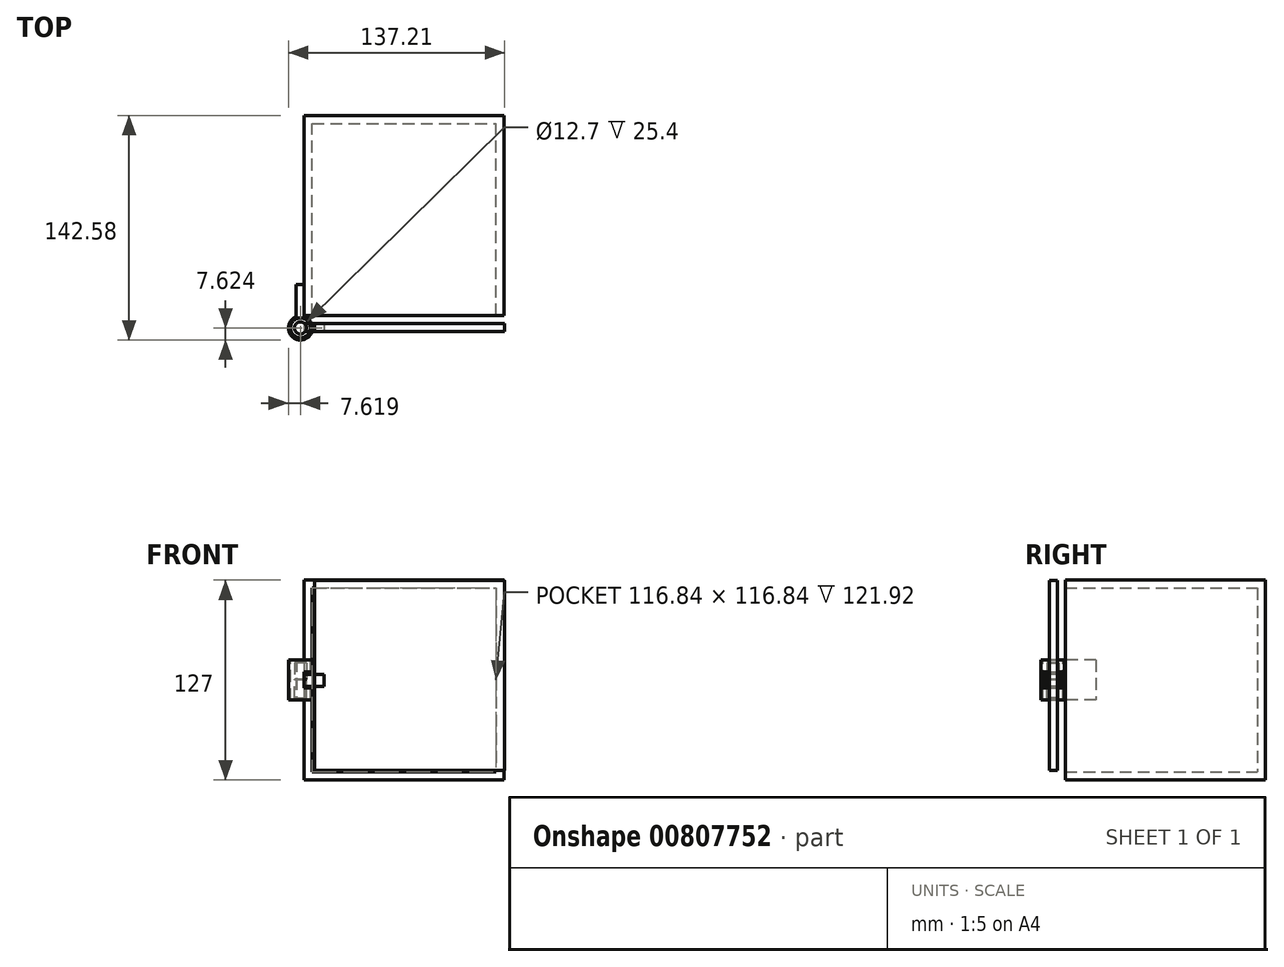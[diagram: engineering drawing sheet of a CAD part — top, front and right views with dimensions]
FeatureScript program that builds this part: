
annotation { "Feature Type Name" : "Feature", "Feature Type Description" : "" }
export const myFeature = defineFeature(function(context is Context, id is Id, definition is map)
    precondition{}
    {
        {
            var Q0;
            Q0=qCreatedBy(makeId("Front.planeOp"),FACE);
            var sketch = newSketch(context, id + "F0", { "sketchPlane" : qUnion([Q0])});
            skLineSegment(sketch, "E0.bottom", {"start": v(-62.85, 63) * mm, "end": v(64.15, 63) * mm});
            skLineSegment(sketch, "E0.top", {"start": v(-62.85, -64) * mm, "end": v(64.15, -64) * mm});
            skLineSegment(sketch, "E0.left", {"start": v(-62.85, 63) * mm, "end": v(-62.85, -64) * mm});
            skLineSegment(sketch, "E0.right", {"start": v(64.15, 63) * mm, "end": v(64.15, -64) * mm});
            skSolve(sketch);
        }
        {
            var Q0;
            Q0 = qSketchRegion(id + "F0", true);
            extrude(context, id + "F1", {"entities" : qUnion([Q0]), "depth" : 127 * mm, "offsetDistance" : 25.4 * mm});
        }
        {
            var Q0;
            Q0=makeQuery(id+"F1.opExtrude","CAP_FACE",FACE,{"disambiguationData":[OSD([sQuery(id+"F0.wireOp",EDGE,"E0.bottom"),sQuery(id+"F0.wireOp",EDGE,"E0.top"),sQuery(id+"F0.wireOp",EDGE,"E0.left"),sQuery(id+"F0.wireOp",EDGE,"E0.right")])],"isStart":false});
            shell(context, id + "F2", {"entities" : qUnion([Q0]), "thickness" : 5.08 * mm});
        }
        {
            var Q0;
            Q0=makeQuery(id+"F1.opExtrude","SWEPT_FACE",FACE,{"disambiguationData":[OSD([sQuery(id+"F0.wireOp",EDGE,"E0.left")])]});
            var sketch = newSketch(context, id + "F3", { "sketchPlane" : qUnion([Q0])});
            skLineSegment(sketch, "E1.bottom", {"start": v(107.48, 12.2) * mm, "end": v(127.8, 12.2) * mm});
            skLineSegment(sketch, "E1.top", {"start": v(107.48, -13.2) * mm, "end": v(127.8, -13.2) * mm});
            skLineSegment(sketch, "E1.left", {"start": v(107.48, 12.2) * mm, "end": v(107.48, -13.2) * mm});
            skLineSegment(sketch, "E1.right", {"start": v(127.8, 12.2) * mm, "end": v(127.8, -13.2) * mm});
            skSolve(sketch);
        }
        {
            var Q0;
            Q0 = qSketchRegion(id + "F3", true);
            extrude(context, id + "F4", {"entities" : qUnion([Q0]), "operationType" : NewBodyOperationType.ADD, "depth" : 5.08 * mm, "offsetDistance" : 25.4 * mm});
        }
        {
            var Q0;
            Q0=makeQuery(id+"F4.opExtrude","SWEPT_FACE",FACE,{"disambiguationData":[OSD([sQuery(id+"F3.wireOp",EDGE,"E1.top")])]});
            var sketch = newSketch(context, id + "F5", { "sketchPlane" : qUnion([Q0])});
            skCircle(sketch, "E2", {"center": v(-65.23, 134.96) * mm, "radius": 7.62 * mm});
            skSolve(sketch);
        }
        {
            var Q0;
            Q0 = qSketchRegion(id + "F5", true);
            extrude(context, id + "F6", {"entities" : qUnion([Q0]), "operationType" : NewBodyOperationType.ADD, "oppositeDirection" : true, "depth" : 25.4 * mm, "offsetDistance" : 25.4 * mm});
        }
        {
            var Q0;
            Q0=makeQuery(id+"F6.boolean.opBoolean","MERGE",FACE,{"derivedFrom":[makeQuery(id+"F4.opExtrude","SWEPT_FACE",FACE,{"disambiguationData":[OSD([sQuery(id+"F3.wireOp",EDGE,"E1.bottom")])]}),makeQuery(id+"F6.opExtrude","CAP_FACE",FACE,{"disambiguationData":[OSD([sQuery(id+"F5.wireOp",EDGE,"E2")])],"isStart":false})]});
            var sketch = newSketch(context, id + "F7", { "sketchPlane" : qUnion([Q0])});
            skCircle(sketch, "E3", {"center": v(-65.23, -134.96) * mm, "radius": 6.35 * mm});
            skSolve(sketch);
        }
        {
            var Q0;
            Q0 = qSketchRegion(id + "F7", true);
            extrude(context, id + "F8", {"entities" : qUnion([Q0]), "operationType" : NewBodyOperationType.REMOVE, "oppositeDirection" : true, "depth" : 65.02 * mm, "offsetDistance" : 25.4 * mm});
        }
        {
            var Q0;
            Q0=makeQuery(id+"F1.opExtrude","CAP_FACE",FACE,{"disambiguationData":[OSD([sQuery(id+"F0.wireOp",EDGE,"E0.bottom"),sQuery(id+"F0.wireOp",EDGE,"E0.top"),sQuery(id+"F0.wireOp",EDGE,"E0.left"),sQuery(id+"F0.wireOp",EDGE,"E0.right")])],"isStart":false});
            var sketch = newSketch(context, id + "F9", { "sketchPlane" : qUnion([Q0])});
            skLineSegment(sketch, "E4.bottom", {"start": v(-62.85, -5.58) * mm, "end": v(-55.23, -5.58) * mm});
            skLineSegment(sketch, "E4.top", {"start": v(-62.85, 4.58) * mm, "end": v(-55.23, 4.58) * mm});
            skLineSegment(sketch, "E4.left", {"start": v(-62.85, -5.58) * mm, "end": v(-62.85, 4.58) * mm});
            skLineSegment(sketch, "E4.right", {"start": v(-55.23, -5.58) * mm, "end": v(-55.23, 4.58) * mm});
            skSolve(sketch);
        }
        {
            var Q0;
            Q0 = qSketchRegion(id + "F9", true);
            extrude(context, id + "F10", {"entities" : qUnion([Q0]), "operationType" : NewBodyOperationType.REMOVE, "depth" : 30.23 * mm, "offsetDistance" : 25.4 * mm});
        }
        {
            var Q0;
            Q0=qCreatedBy(makeId("Top.planeOp"),FACE);
            var sketch = newSketch(context, id + "F11", { "sketchPlane" : qUnion([Q0])});
            skCircle(sketch, "E5", {"center": v(-65.23, -134.96) * mm, "radius": 3.81 * mm});
            skSolve(sketch);
        }
        {
            var Q0;
            Q0 = qSketchRegion(id + "F11", true);
            extrude(context, id + "F12", {"entities" : qUnion([Q0]), "depth" : 10.4 * mm, "offsetDistance" : 25.4 * mm});
        }
        {
            var Q0;
            Q0=makeQuery(id+"F12.opExtrude","CAP_FACE",FACE,{"disambiguationData":[OSD([sQuery(id+"F11.wireOp",EDGE,"E5")])],"isStart":true});
            cPlane(context, id + "F13", {"entities" : qUnion([Q0]), "cplaneType" : CPlaneType.OFFSET, "offset" : 0 * mm, "width" : 152.4 * mm, "height" : 152.4 * mm});
        }
        {
            var Q0;
            Q0=makeQuery(id+"F2.opShell","OFFSET_FACE",FACE,{"disambiguationData":[OSD([sQuery(id+"F0.wireOp",EDGE,"E0.bottom"),sQuery(id+"F0.wireOp",EDGE,"E0.top"),sQuery(id+"F0.wireOp",EDGE,"E0.left"),sQuery(id+"F0.wireOp",EDGE,"E0.right")])]});
            cPlane(context, id + "F14", {"entities" : qUnion([Q0]), "cplaneType" : CPlaneType.OFFSET, "offset" : 127 * mm, "width" : 152.4 * mm, "height" : 152.4 * mm});
        }
        {
            var Q0;
            Q0=qCreatedBy(id+"F14.planeOp",FACE);
            var sketch = newSketch(context, id + "F15", { "sketchPlane" : qUnion([Q0])});
            skLineSegment(sketch, "E6.bottom", {"start": v(-56.29, 62.83) * mm, "end": v(64.36, 62.83) * mm});
            skLineSegment(sketch, "E6.top", {"start": v(-56.29, -57.82) * mm, "end": v(64.36, -57.82) * mm});
            skLineSegment(sketch, "E6.left", {"start": v(-56.29, 62.83) * mm, "end": v(-56.29, -57.82) * mm});
            skLineSegment(sketch, "E6.right", {"start": v(64.36, 62.83) * mm, "end": v(64.36, -57.82) * mm});
            skSolve(sketch);
        }
        {
            var Q0;
            Q0=makeQuery(id+"F15.imprint","IMPRINT",FACE,{"disambiguationData":[TD([[makeQuery(id+"F15.imprint","IMPRINT",EDGE,{"derivedFrom":sQuery(id+"F15.wireOp",EDGE,"E6.bottom")}),-1.0]])]});
            extrude(context, id + "F16", {"entities" : qUnion([Q0]), "depth" : 5.08 * mm, "offsetDistance" : 25.4 * mm});
        }
        {
            var Q0;
            Q0=makeQuery(id+"F16.opExtrude","CAP_FACE",FACE,{"disambiguationData":[OSD([sQuery(id+"F15.wireOp",EDGE,"E6.bottom"),sQuery(id+"F15.wireOp",EDGE,"E6.top"),sQuery(id+"F15.wireOp",EDGE,"E6.left"),sQuery(id+"F15.wireOp",EDGE,"E6.right")])],"isStart":false});
            var sketch = newSketch(context, id + "F17", { "sketchPlane" : qUnion([Q0])});
            skPoint(sketch, "E7.firstSnap0", {"position": v(-56.29, 2.5) * mm});
            skLineSegment(sketch, "E7.bottom", {"start": v(-50.3, 3.14) * mm, "end": v(-63, 3.14) * mm});
            skLineSegment(sketch, "E7.top", {"start": v(-50.3, -4.48) * mm, "end": v(-63, -4.48) * mm});
            skLineSegment(sketch, "E7.left", {"start": v(-50.3, 3.14) * mm, "end": v(-50.3, -4.48) * mm});
            skLineSegment(sketch, "E7.right", {"start": v(-63, 3.14) * mm, "end": v(-63, -4.48) * mm});
            skSolve(sketch);
        }
        {
            var Q0;
            Q0 = qSketchRegion(id + "F17", true);
            extrude(context, id + "F18", {"entities" : qUnion([Q0]), "oppositeDirection" : true, "depth" : 5.08 * mm, "offsetDistance" : 25.4 * mm});
        }
        {
            var Q0;
            Q0=qCreatedBy(id+"F13.planeOp",FACE);
            var sketch = newSketch(context, id + "F19", { "sketchPlane" : qUnion([Q0])});
            skCircle(sketch, "E8", {"center": v(-65.23, 134.96) * mm, "radius": 3.8 * mm});
            skSolve(sketch);
        }
        {
            var Q0;
            Q0 = qSketchRegion(id + "F19", true);
            extrude(context, id + "F20", {"entities" : qUnion([Q0]), "depth" : 11.94 * mm, "offsetDistance" : 25.4 * mm});
        }
    });
